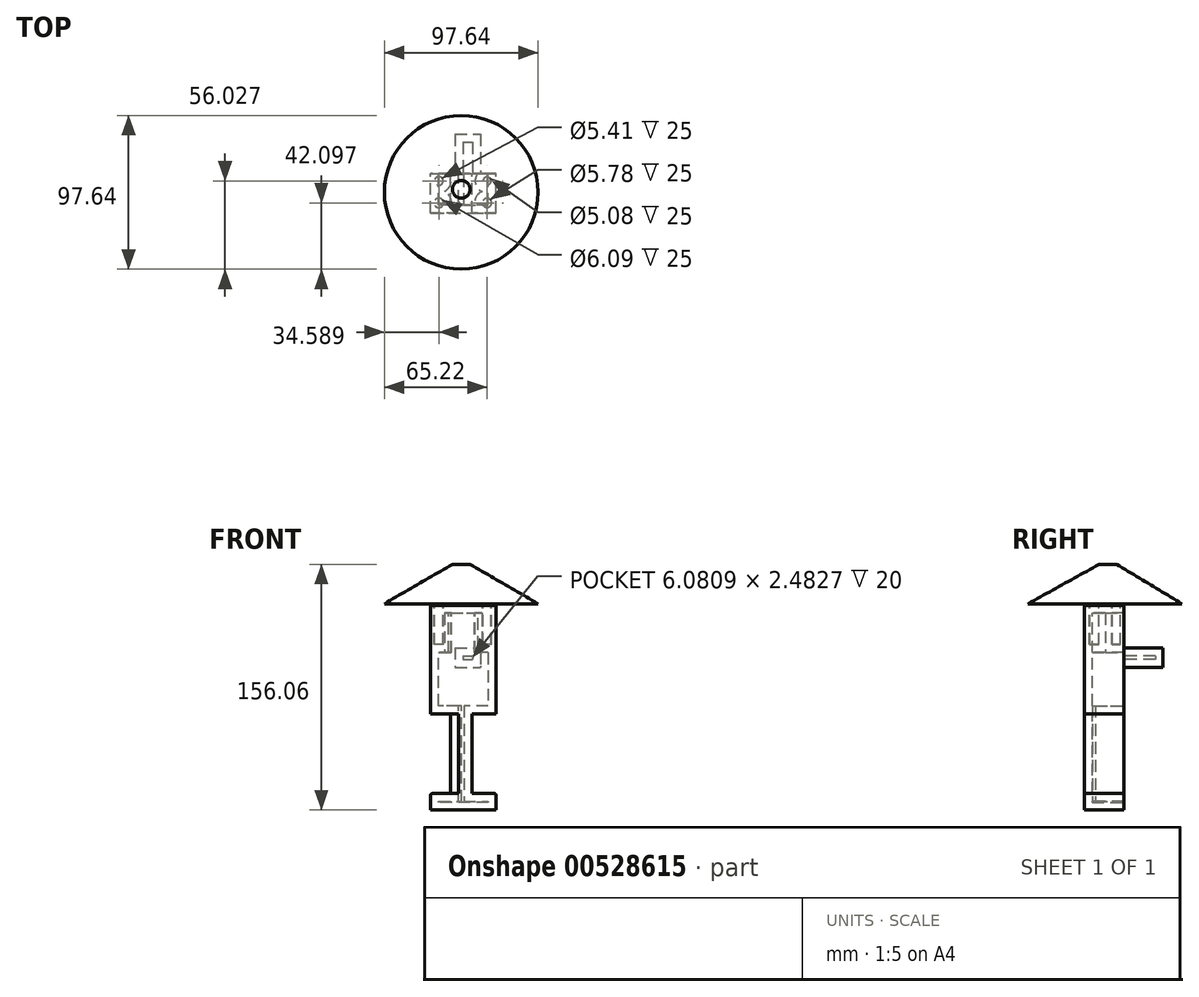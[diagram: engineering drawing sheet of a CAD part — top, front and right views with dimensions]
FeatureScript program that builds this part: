
annotation { "Feature Type Name" : "Feature", "Feature Type Description" : "" }
export const myFeature = defineFeature(function(context is Context, id is Id, definition is map)
    precondition{}
    {
        {
            var Q0;
            Q0=qCreatedBy(makeId("Front.planeOp"),FACE);
            var sketch = newSketch(context, id + "F0", { "sketchPlane" : qUnion([Q0])});
            skLineSegment(sketch, "E0", {"start": v(-19.4, 96.35) * mm, "end": v(22.14, 96.35) * mm});
            skLineSegment(sketch, "E1", {"start": v(22.14, 96.35) * mm, "end": v(22.14, 27.5) * mm});
            skLineSegment(sketch, "E2", {"start": v(22.14, 27.5) * mm, "end": v(6.72, 27.5) * mm});
            skLineSegment(sketch, "E3", {"start": v(6.72, 27.5) * mm, "end": v(6.72, -23.26) * mm});
            skLineSegment(sketch, "E4", {"start": v(6.72, -23.26) * mm, "end": v(22.14, -23.26) * mm});
            skLineSegment(sketch, "E5", {"start": v(22.14, -23.26) * mm, "end": v(22.14, -33.71) * mm});
            skLineSegment(sketch, "E6", {"start": v(22.14, -33.71) * mm, "end": v(-19.4, -33.71) * mm});
            skLineSegment(sketch, "E7", {"start": v(-19.4, -33.71) * mm, "end": v(-19.4, -23.26) * mm});
            skLineSegment(sketch, "E8", {"start": v(-19.4, -23.26) * mm, "end": v(-6.72, -23.26) * mm});
            skLineSegment(sketch, "E9", {"start": v(-6.72, -23.26) * mm, "end": v(-6.72, 27.5) * mm});
            skLineSegment(sketch, "E10", {"start": v(-6.72, 27.5) * mm, "end": v(-19.4, 27.5) * mm});
            skLineSegment(sketch, "E11", {"start": v(-19.4, 27.5) * mm, "end": v(-19.4, 96.35) * mm});
            skSolve(sketch);
        }
        {
            var Q0;
            Q0=makeQuery(id+"F0.imprint","IMPRINT",FACE,{"disambiguationData":[TD([[makeQuery(id+"F0.imprint","IMPRINT",EDGE,{"derivedFrom":sQuery(id+"F0.wireOp",EDGE,"E0")}),-1.0]])]});
            extrude(context, id + "F1", {"entities" : qUnion([Q0]), "depth" : 25 * mm, "offsetDistance" : 25 * mm});
        }
        {
            var Q0;
            Q0=makeQuery(id+"F1.opExtrude","SWEPT_FACE",FACE,{"disambiguationData":[OSD([sQuery(id+"F0.wireOp",EDGE,"E0")])]});
            var sketch = newSketch(context, id + "F2", { "sketchPlane" : qUnion([Q0])});
            skCircle(sketch, "E12", {"center": v(-14.23, -4.72) * mm, "radius": 2.7 * mm});
            skCircle(sketch, "E13", {"center": v(-14.23, -18.65) * mm, "radius": 3.04 * mm});
            skCircle(sketch, "E14", {"center": v(16.4, -4.72) * mm, "radius": 2.54 * mm});
            skCircle(sketch, "E15", {"center": v(16.4, -18.65) * mm, "radius": 2.89 * mm});
            skSolve(sketch);
        }
        {
            var Q0;
            Q0=makeQuery(id+"F2.imprint","IMPRINT",FACE,{"disambiguationData":[TD([[makeQuery(id+"F2.imprint","IMPRINT",EDGE,{"derivedFrom":sQuery(id+"F2.wireOp",EDGE,"E12")}),1.0]])]});
            var Q1;
            Q1=makeQuery(id+"F2.imprint","IMPRINT",FACE,{"disambiguationData":[TD([[makeQuery(id+"F2.imprint","IMPRINT",EDGE,{"derivedFrom":sQuery(id+"F2.wireOp",EDGE,"E13")}),1.0]])]});
            var Q2;
            Q2=makeQuery(id+"F2.imprint","IMPRINT",FACE,{"disambiguationData":[TD([[makeQuery(id+"F2.imprint","IMPRINT",EDGE,{"derivedFrom":sQuery(id+"F2.wireOp",EDGE,"E14")}),1.0]])]});
            var Q3;
            Q3=makeQuery(id+"F2.imprint","IMPRINT",FACE,{"disambiguationData":[TD([[makeQuery(id+"F2.imprint","IMPRINT",EDGE,{"derivedFrom":sQuery(id+"F2.wireOp",EDGE,"E15")}),1.0]])]});
            var Q4;
            Q4=makeQuery(id+"F1.opExtrude","SWEPT_FACE",FACE,{"disambiguationData":[OSD([sQuery(id+"F0.wireOp",EDGE,"E6")])]});
            extrude(context, id + "F3", {"entities" : qUnion([Q0, Q1, Q2, Q3]), "operationType" : NewBodyOperationType.REMOVE, "oppositeDirection" : true, "depth" : 25 * mm, "endBoundEntityFace" : qUnion([Q4]), "offsetDistance" : 25 * mm});
        }
        {
            var Q0;
            Q0=makeQuery(id+"F1.opExtrude","CAP_FACE",FACE,{"disambiguationData":[OSD([sQuery(id+"F0.wireOp",EDGE,"E0"),sQuery(id+"F0.wireOp",EDGE,"E1"),sQuery(id+"F0.wireOp",EDGE,"E2"),sQuery(id+"F0.wireOp",EDGE,"E3"),sQuery(id+"F0.wireOp",EDGE,"E4"),sQuery(id+"F0.wireOp",EDGE,"E5"),sQuery(id+"F0.wireOp",EDGE,"E6"),sQuery(id+"F0.wireOp",EDGE,"E7"),sQuery(id+"F0.wireOp",EDGE,"E8"),sQuery(id+"F0.wireOp",EDGE,"E9"),sQuery(id+"F0.wireOp",EDGE,"E10"),sQuery(id+"F0.wireOp",EDGE,"E11")])],"isStart":true});
            var sketch = newSketch(context, id + "F4", { "sketchPlane" : qUnion([Q0])});
            skLineSegment(sketch, "E16.bottom", {"start": v(3.9, 69.34) * mm, "end": v(-12.19, 69.34) * mm});
            skLineSegment(sketch, "E16.top", {"start": v(3.9, 56.86) * mm, "end": v(-12.19, 56.86) * mm});
            skLineSegment(sketch, "E16.left", {"start": v(3.9, 69.34) * mm, "end": v(3.9, 56.86) * mm});
            skLineSegment(sketch, "E16.right", {"start": v(-12.19, 69.34) * mm, "end": v(-12.19, 56.86) * mm});
            skPoint(sketch, "E16.middle", {"position": v(-4.15, 63.1) * mm});
            skSolve(sketch);
        }
        {
            var Q0;
            Q0=makeQuery(id+"F4.imprint","IMPRINT",FACE,{"disambiguationData":[TD([[makeQuery(id+"F4.imprint","IMPRINT",EDGE,{"derivedFrom":sQuery(id+"F4.wireOp",EDGE,"E16.bottom")}),1.0]])]});
            extrude(context, id + "F5", {"entities" : qUnion([Q0]), "operationType" : NewBodyOperationType.ADD, "depth" : 25 * mm, "offsetDistance" : 25 * mm});
        }
        {
            var Q0;
            Q0=makeQuery(id+"F1.opExtrude","SWEPT_FACE",FACE,{"disambiguationData":[OSD([sQuery(id+"F0.wireOp",EDGE,"E0")])]});
            cPlane(context, id + "F6", {"entities" : qUnion([Q0]), "cplaneType" : CPlaneType.OFFSET, "offset" : 1 * mm, "width" : 150 * mm, "height" : 150 * mm});
        }
        {
            var Q0;
            Q0=qCreatedBy(id+"F6.planeOp",FACE);
            var sketch = newSketch(context, id + "F7", { "sketchPlane" : qUnion([Q0])});
            skCircle(sketch, "E17", {"center": v(0, -11.93) * mm, "radius": 48.82 * mm});
            skSolve(sketch);
        }
        {
            var Q0;
            Q0=qCreatedBy(id+"F6.planeOp",FACE);
            cPlane(context, id + "F8", {"entities" : qUnion([Q0]), "cplaneType" : CPlaneType.OFFSET, "offset" : 25 * mm, "width" : 150 * mm, "height" : 150 * mm});
        }
        {
            var Q0;
            Q0=qCreatedBy(id+"F8.planeOp",FACE);
            var sketch = newSketch(context, id + "F9", { "sketchPlane" : qUnion([Q0])});
            skCircle(sketch, "E18", {"center": v(0, -10.04) * mm, "radius": 5.64 * mm});
            skSolve(sketch);
        }
        {
            var Q0;
            Q0=makeQuery(id+"F7.imprint","IMPRINT",FACE,{"disambiguationData":[TD([[makeQuery(id+"F7.imprint","IMPRINT",EDGE,{"derivedFrom":sQuery(id+"F7.wireOp",EDGE,"E17")}),1.0]])]});
            var Q1;
            Q1=makeQuery(id+"F9.imprint","IMPRINT",FACE,{"disambiguationData":[TD([[makeQuery(id+"F9.imprint","IMPRINT",EDGE,{"derivedFrom":sQuery(id+"F9.wireOp",EDGE,"E18")}),1.0]])]});
            loft(context, id + "F10", {"sheetProfilesArray" : [{ "sheetProfileEntities" : qUnion([Q0]) }, { "sheetProfileEntities" : qUnion([Q1]) }]});
        }
        {
            var Q0;
            Q0=makeQuery(id+"F1.opExtrude","SWEPT_EDGE",EDGE,{"disambiguationData":[OSD([sQuery(id+"F0.wireOp",EDGE,"E4"),sQuery(id+"F0.wireOp",EDGE,"E5")])]});
            var Q1;
            Q1=makeQuery(id+"F1.opExtrude","SWEPT_EDGE",EDGE,{"disambiguationData":[OSD([sQuery(id+"F0.wireOp",EDGE,"E7"),sQuery(id+"F0.wireOp",EDGE,"E8")])]});
            fillet(context, id + "F11", {"entities" : qUnion([Q0, Q1]), "radius" : 1 * mm, "tangentPropagation" : true, "allowEdgeOverflow" : false});
        }
        {
            var Q0;
            Q0=makeQuery(id+"F1.opExtrude","CAP_EDGE",EDGE,{"disambiguationData":[OSD([sQuery(id+"F0.wireOp",EDGE,"E9")])],"isStart":false});
            chamfer(context, id + "F12", {"entities" : qUnion([Q0]), "width" : 5 * mm, "tangentPropagation" : true});
        }
        {
            var Q0;
            Q0=makeQuery(id+"F1.opExtrude","CAP_FACE",FACE,{"disambiguationData":[OSD([sQuery(id+"F0.wireOp",EDGE,"E0"),sQuery(id+"F0.wireOp",EDGE,"E1"),sQuery(id+"F0.wireOp",EDGE,"E2"),sQuery(id+"F0.wireOp",EDGE,"E3"),sQuery(id+"F0.wireOp",EDGE,"E4"),sQuery(id+"F0.wireOp",EDGE,"E5"),sQuery(id+"F0.wireOp",EDGE,"E6"),sQuery(id+"F0.wireOp",EDGE,"E7"),sQuery(id+"F0.wireOp",EDGE,"E8"),sQuery(id+"F0.wireOp",EDGE,"E9"),sQuery(id+"F0.wireOp",EDGE,"E10"),sQuery(id+"F0.wireOp",EDGE,"E11")])],"isStart":true});
            shell(context, id + "F13", {"entities" : qUnion([Q0]), "thickness" : 5 * mm});
        }
    });
